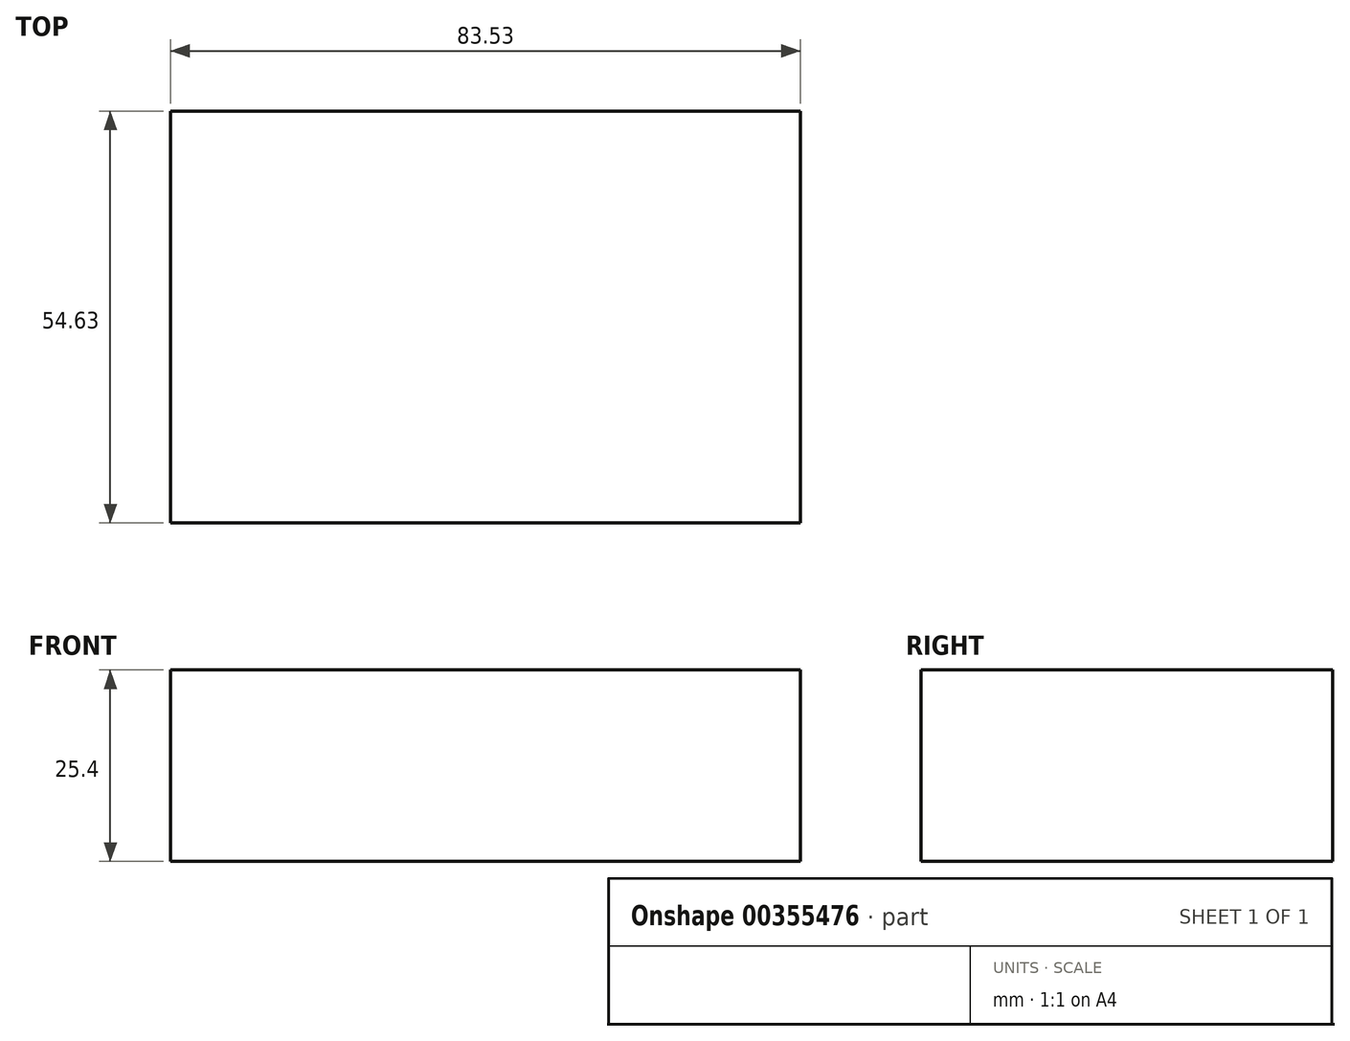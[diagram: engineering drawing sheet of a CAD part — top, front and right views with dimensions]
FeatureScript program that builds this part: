
annotation { "Feature Type Name" : "Feature", "Feature Type Description" : "" }
export const myFeature = defineFeature(function(context is Context, id is Id, definition is map)
    precondition{}
    {
        {
            var Q0;
            Q0=qCreatedBy(makeId("Top.planeOp"),FACE);
            var sketch = newSketch(context, id + "F0", { "sketchPlane" : qUnion([Q0])});
            skLineSegment(sketch, "E0.bottom", {"start": v(-36.18, 33.63) * mm, "end": v(47.35, 33.63) * mm});
            skLineSegment(sketch, "E0.top", {"start": v(-36.18, -21) * mm, "end": v(47.35, -21) * mm});
            skLineSegment(sketch, "E0.left", {"start": v(-36.18, 33.63) * mm, "end": v(-36.18, -21) * mm});
            skLineSegment(sketch, "E0.right", {"start": v(47.35, 33.63) * mm, "end": v(47.35, -21) * mm});
            skSolve(sketch);
        }
        {
            var Q0;
            Q0=makeQuery(id+"F0.imprint","IMPRINT",FACE,{"disambiguationData":[TD([[makeQuery(id+"F0.imprint","IMPRINT",EDGE,{"derivedFrom":sQuery(id+"F0.wireOp",EDGE,"E0.bottom")}),-1.0]])]});
            extrude(context, id + "F1", {"entities" : qUnion([Q0]), "depth" : 25.4 * mm});
        }
    });
